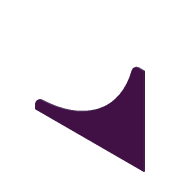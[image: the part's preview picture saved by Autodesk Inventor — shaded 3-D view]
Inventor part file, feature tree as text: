
AUTODESK INVENTOR PART (.ipt)
format: ipt  version: 2012 (Build 160160000, 160)  size: 77,312 bytes
history: native  units: in
note: dims shown in document units (in); Inventor stores cm internally (conversion verified against a paired STEP export)
features: extrude x1, fillet x1, sketch x1
ambient origin geometry x8: Origin, YZ Plane, XZ Plane, XY Plane, X Axis, Y Axis, Z Axis, Center Point
bodies: Solid1 (feature_tree)
feature tree (3):
  extrude  "Extrusion1"  Depth=6.0in
  fillet  "Fillet1"  Radius=0.75in
  sketch  "Sketch1"  dims[d0=0.75in d1=6.0in d2=0.75in d3=7.5in d4=0.0625in d5=0.0in d6=0.5in]
